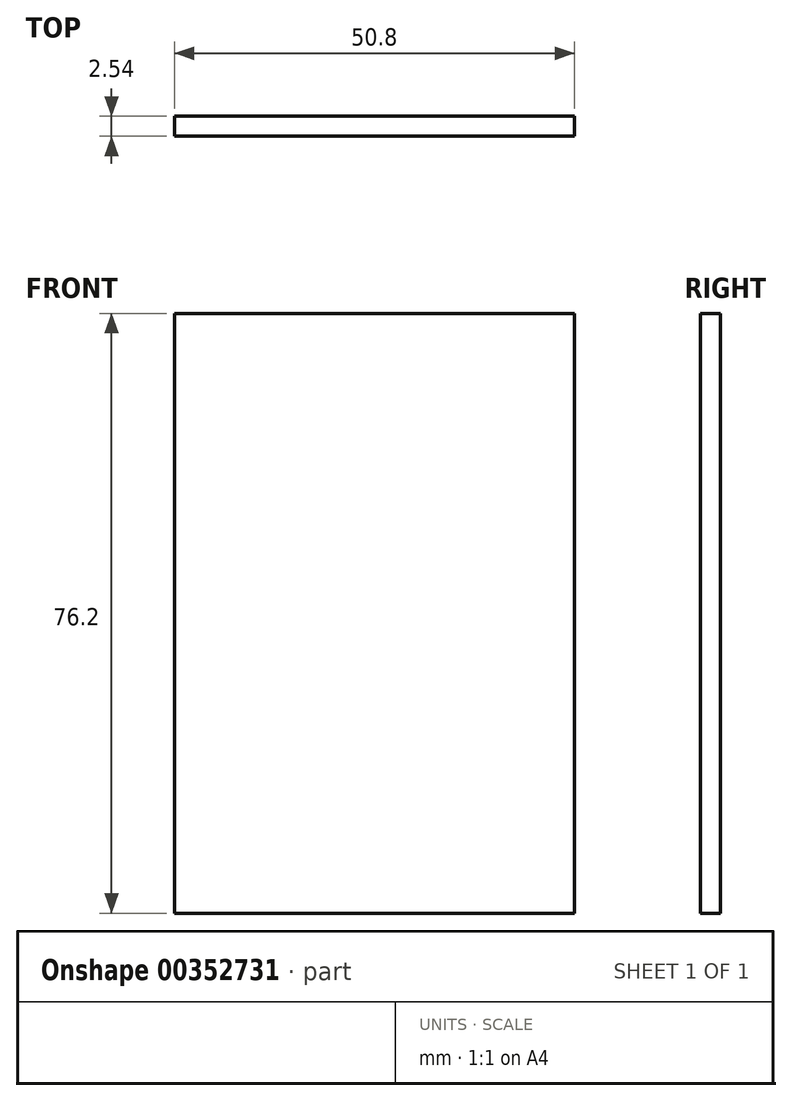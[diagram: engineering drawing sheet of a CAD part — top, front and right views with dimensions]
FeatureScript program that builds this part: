
annotation { "Feature Type Name" : "Feature", "Feature Type Description" : "" }
export const myFeature = defineFeature(function(context is Context, id is Id, definition is map)
    precondition{}
    {
        {
            var Q0;
            Q0=qCreatedBy(makeId("Front.planeOp"),FACE);
            var sketch = newSketch(context, id + "F0", { "sketchPlane" : qUnion([Q0])});
            skLineSegment(sketch, "E0.bottom", {"start": v(25.4, -38.1) * mm, "end": v(-25.4, -38.1) * mm});
            skLineSegment(sketch, "E0.top", {"start": v(25.4, 38.1) * mm, "end": v(-25.4, 38.1) * mm});
            skLineSegment(sketch, "E0.left", {"start": v(25.4, -38.1) * mm, "end": v(25.4, 38.1) * mm});
            skLineSegment(sketch, "E0.right", {"start": v(-25.4, -38.1) * mm, "end": v(-25.4, 38.1) * mm});
            skPoint(sketch, "E0.middle", {"position": v(0, 0) * mm});
            skSolve(sketch);
        }
        {
            var Q0;
            Q0=makeQuery(id+"F0.imprint","IMPRINT",FACE,{"disambiguationData":[TD([[makeQuery(id+"F0.imprint","IMPRINT",EDGE,{"derivedFrom":sQuery(id+"F0.wireOp",EDGE,"E0.bottom")}),-1.0]])]});
            extrude(context, id + "F1", {"entities" : qUnion([Q0]), "depth" : 2.54 * mm});
        }
    });
